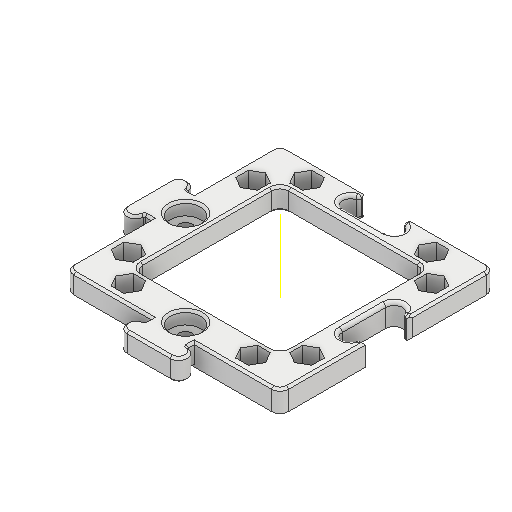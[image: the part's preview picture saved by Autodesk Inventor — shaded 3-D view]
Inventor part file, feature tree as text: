
AUTODESK INVENTOR PART (.ipt)
format: ipt  version: 2022 (Build 260153000, 153)  size: 544,768 bytes
history: native  units: mm
features: sketch x5, extrude x4, projected_geometry x3, mirror x2, other x1, pattern_circular x1, hole x1, chamfer x1, fillet x1
ambient origin geometry x8: Origin, YZ Plane, XZ Plane, XY Plane, X Axis, Y Axis, Z Axis, Center Point
bodies: Volumenkörper1 (feature_tree)
feature tree (19):
  extrude  "Extrusion1"  TaperAngle=0.0deg  [1 undecoded]
  mirror  "Mirror6"
  mirror  "Mirror7"
  extrude  "Extrusion13"  TaperAngle=0.0deg  [1 undecoded]
  extrude  "Extrusion14"  TaperAngle=0.0deg  [1 undecoded]
  other  "Work Axis4"
  pattern_circular  "Circular Pattern6"  [2 undecoded]
  hole  "Hole7"  [1 undecoded]
  chamfer  "Fase4"  [1 undecoded]
  fillet  "Rundung5"  [1 undecoded]
  extrude  "Extrusion18"  Depth=3.0mm
  sketch  "Skizze1"  dims[d5=0.0mm d6=0.0mm]
  sketch  "Sketch26"  dims[d7=0.0mm d8=0.0mm]
  projected_geometry  "Projected Loop21"
  sketch  "Sketch28"  dims[d9=0.0mm d13=0.0mm]
  sketch  "Sketch29"  dims[d14=0.0mm]
  projected_geometry  "Projected Loop24"
  projected_geometry  "Projizierte Kontur27"
  sketch  "Skizze33"  dims[d20=0.0mm d21=0.0mm d22=0.0mm d23=0.0mm d24=0.0mm d25=3.0mm d26=0.0mm d27=0.0mm d28=0.0mm d29=0.0mm d30=0.0mm d31=0.0mm d32=0.0mm d33=0.0mm d34=0.0mm d46=0.0mm d47=0.0mm d48=0.0mm d49=-10.0mm d50=0.0mm d51=0.0mm d52=0.0mm d53=0.0mm d54=0.0mm d55=0.0mm d56=0.0mm d57=0.0mm d58=0.0mm d59=0.0mm d77=2.65mm d82=2.65mm d222=0.5mm d236=5.3mm d278=25.0mm d279=25.0mm d2=8.0mm d281=8.0mm d282=2.0mm d286=5.1mm d290=20.8mm d292=2.0mm d293=5.6mm d298=10.0mm d299=0.0mm d300=2.0mm d301=0.25mm d302=10.0mm d303=0.0mm d308=20.0mm d309=90.0deg d313=6.3mm d314=6.3mm d319=7.78mm d320=5.0mm d322=5.0mm d323=3.2mm d324=6.0mm d325=7.0mm d326=3.0mm d327=90.0deg d328=8.0mm d329=20.594885mm d331=0.0mm d332=0.0mm d360=0.5mm d361=2.0mm d362=45.0deg d365=7.0mm d367=7.0mm d369=4.2mm d370=0.0mm d380=45.0deg d384=0.75mm d385=5.0mm d386=5.0mm d387=2.0mm d388=0.25mm d391=0.1mm d392=5.05mm d393=5.05mm d394=1.96mm d396=5.45mm d397=7.05mm d398=10.0mm d399=0.0mm]
note: 8 required parameter values undecoded (feature->parameter linkage not recoverable at this tier; creation-order binding heuristic only, values carry confidence <= 0.55)
